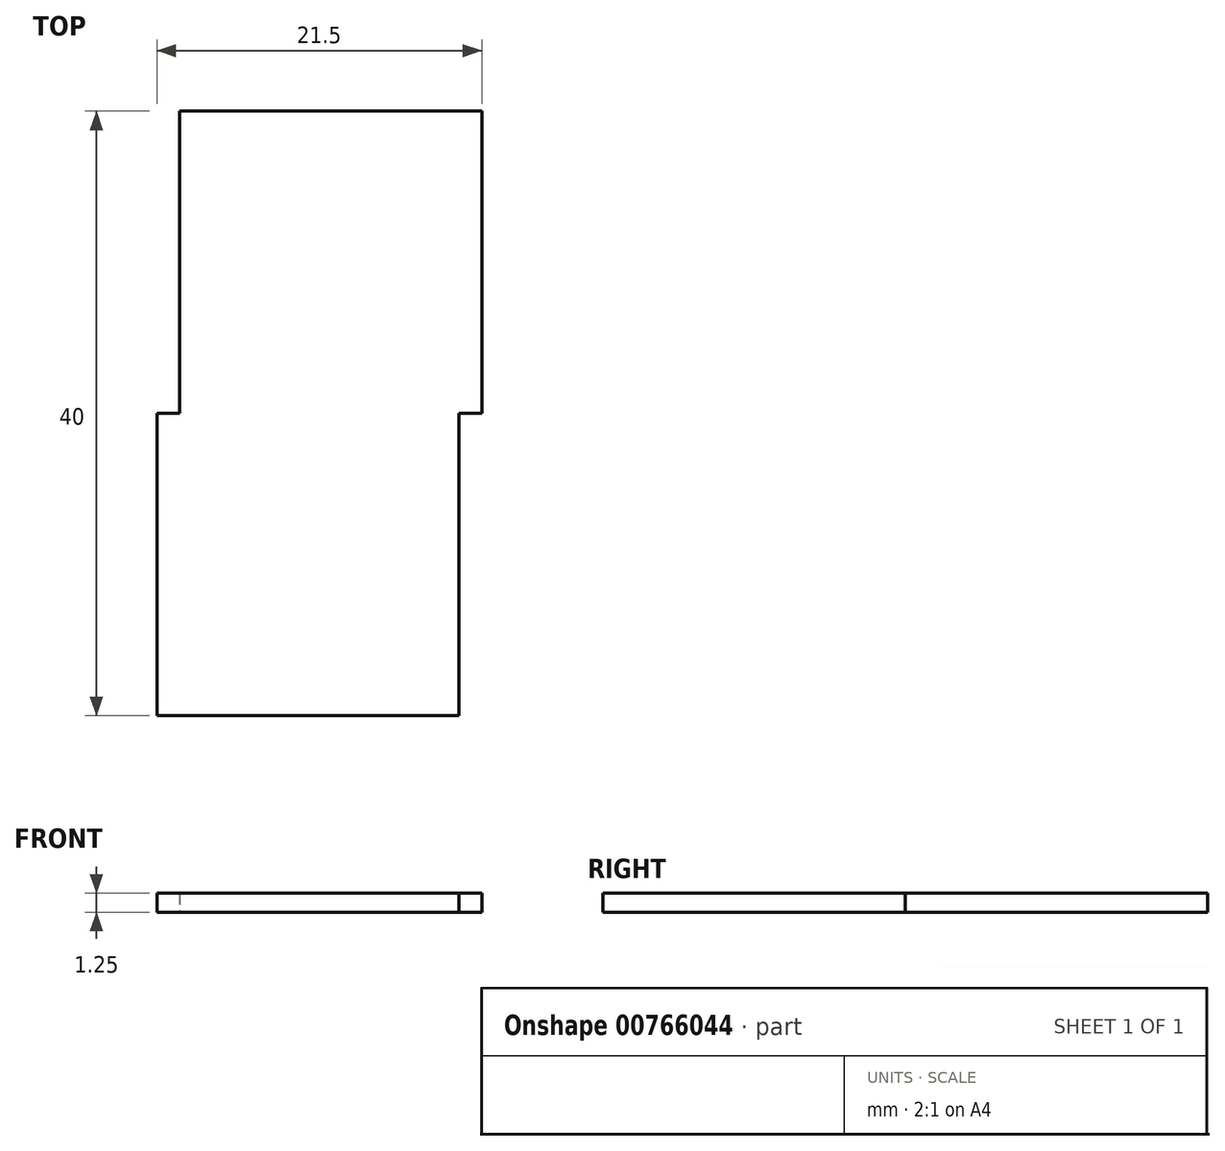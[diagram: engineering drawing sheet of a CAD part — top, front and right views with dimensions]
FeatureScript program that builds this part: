
annotation { "Feature Type Name" : "Feature", "Feature Type Description" : "" }
export const myFeature = defineFeature(function(context is Context, id is Id, definition is map)
    precondition{}
    {
        {
            var Q0;
            Q0=qCreatedBy(makeId("Top.planeOp"),FACE);
            var sketch = newSketch(context, id + "F0", { "sketchPlane" : qUnion([Q0])});
            skLineSegment(sketch, "E0.bottom", {"start": v(0, 0) * mm, "end": v(-20, 0) * mm});
            skLineSegment(sketch, "E0.top", {"start": v(-18.5, 20) * mm, "end": v(-20, 20) * mm});
            skLineSegment(sketch, "E0.left", {"start": v(0, 0) * mm, "end": v(0, 20) * mm});
            skLineSegment(sketch, "E0.right", {"start": v(-20, 0) * mm, "end": v(-20, 20) * mm});
            skLineSegment(sketch, "E1", {"start": v(-18.5, 20) * mm, "end": v(-18.5, 40) * mm});
            skLineSegment(sketch, "E2", {"start": v(-18.5, 40) * mm, "end": v(1.5, 40) * mm});
            skLineSegment(sketch, "E3", {"start": v(1.5, 40) * mm, "end": v(1.5, 20) * mm});
            skLineSegment(sketch, "E4", {"start": v(0, 20) * mm, "end": v(1.5, 20) * mm});
            skSolve(sketch);
        }
        {
            var Q0;
            Q0=makeQuery(id+"F0.imprint","IMPRINT",FACE,{"disambiguationData":[TD([[makeQuery(id+"F0.imprint","IMPRINT",EDGE,{"derivedFrom":sQuery(id+"F0.wireOp",EDGE,"E0.bottom")}),-1.0]])]});
            extrude(context, id + "F1", {"entities" : qUnion([Q0]), "depth" : 1.25 * mm, "offsetDistance" : 25 * mm});
        }
    });
